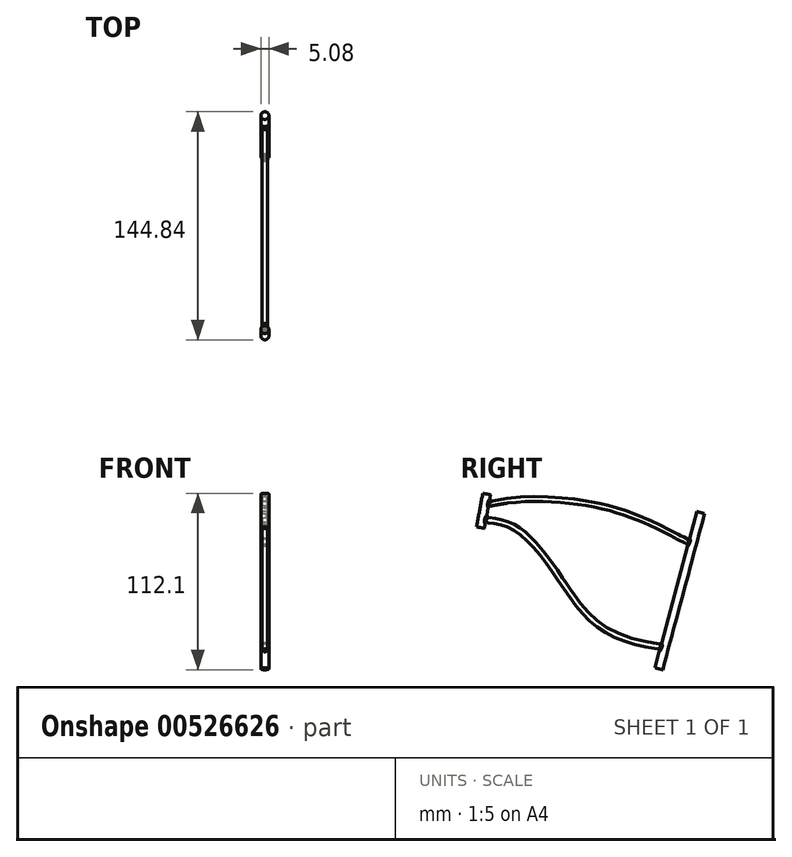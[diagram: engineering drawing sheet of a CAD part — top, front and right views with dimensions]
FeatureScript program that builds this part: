
annotation { "Feature Type Name" : "Feature", "Feature Type Description" : "" }
export const myFeature = defineFeature(function(context is Context, id is Id, definition is map)
    precondition{}
    {
        {
            var Q0;
            Q0=qCreatedBy(makeId("Right.planeOp"),FACE);
            var sketch = newSketch(context, id + "F0", { "sketchPlane" : qUnion([Q0])});
            skLineSegment(sketch, "E0", {"start": v(64.7, 35.74) * mm, "end": v(38.09, -63.45) * mm});
            skLineSegment(sketch, "E1", {"start": v(-71.22, 47.53) * mm, "end": v(-75.2, 26.24) * mm});
            skFitSpline(sketch, "E2", {"points": [v(59.3, 15.64) * mm, v(3.87, 39.19) * mm, v(-72.53, 40.51) * mm], "startDerivative": vector(-133.27, 70.5) * mm, "endDerivative": vector(-137.17, -35.71) * mm});
            skFitSpline(sketch, "E3", {"points": [v(-74.24, 31.39) * mm, v(-54.53, 26.67) * mm, v(-28.9, 0) * mm, v(-2.09, -34.12) * mm, v(41.72, -49.91) * mm], "startDerivative": vector(94.97, -12.02) * mm, "endDerivative": vector(194.9, -25.15) * mm});
            skLineSegment(sketch, "E4", {"start": v(64.7, 35.74) * mm, "end": v(81.02, 31.37) * mm});
            skLineSegment(sketch, "E5", {"start": v(64.7, 35.74) * mm, "end": v(52.13, 39.11) * mm});
            skLineSegment(sketch, "E6", {"start": v(-71.22, 47.53) * mm, "end": v(-80.57, 49.28) * mm});
            skSolve(sketch);
        }
        {
            var Q0;
            Q0=sQuery(id+"F0.wireOp",EDGE,"E1");
            extrude(context, id + "F1", {"bodyType" : ToolBodyType.SURFACE, "surfaceEntities" : qUnion([Q0]), "endBound" : BoundingType.SYMMETRIC, "depth" : 25.4 * mm, "offsetDistance" : 25.4 * mm});
        }
        {
            var Q0;
            Q0=makeQuery(id+"F1.opExtrude","SWEPT_FACE",FACE,{"disambiguationData":[OSD([sQuery(id+"F0.wireOp",EDGE,"E1")])]});
            var sketch = newSketch(context, id + "F2", { "sketchPlane" : qUnion([Q0])});
            skCircle(sketch, "E7", {"center": v(0, 26.48) * mm, "radius": 1.65 * mm});
            skCircle(sketch, "E8", {"center": v(0, 17.23) * mm, "radius": 1.65 * mm});
            skSolve(sketch);
        }
        {
            var Q0;
            Q0=makeQuery(id+"F2.imprint","IMPRINT",FACE,{"disambiguationData":[TD([[makeQuery(id+"F2.imprint","IMPRINT",EDGE,{"derivedFrom":sQuery(id+"F2.wireOp",EDGE,"E7")}),1.0]])]});
            var Q1;
            Q1=sQuery(id+"F0.wireOp",EDGE,"E2");
            sweep(context, id + "F3", {"profiles" : qUnion([Q0]), "path" : qUnion([Q1])});
        }
        {
            var Q0;
            Q0=makeQuery(id+"F2.imprint","IMPRINT",FACE,{"disambiguationData":[TD([[makeQuery(id+"F2.imprint","IMPRINT",EDGE,{"derivedFrom":sQuery(id+"F2.wireOp",EDGE,"E8")}),1.0]])]});
            var Q1;
            Q1=sQuery(id+"F0.wireOp",EDGE,"E3");
            sweep(context, id + "F4", {"profiles" : qUnion([Q0]), "path" : qUnion([Q1])});
        }
        {
            var Q0;
            Q0=sQuery(id+"F0.wireOp",EDGE,"E4");
            extrude(context, id + "F5", {"bodyType" : ToolBodyType.SURFACE, "surfaceEntities" : qUnion([Q0]), "endBound" : BoundingType.SYMMETRIC, "depth" : 25.4 * mm, "offsetDistance" : 25.4 * mm});
        }
        {
            var Q0;
            Q0=makeQuery(id+"F5.opExtrude","SWEPT_FACE",FACE,{"disambiguationData":[OSD([sQuery(id+"F0.wireOp",EDGE,"E4")])]});
            var sketch = newSketch(context, id + "F6", { "sketchPlane" : qUnion([Q0])});
            skCircle(sketch, "E9", {"center": v(0, -53.22) * mm, "radius": 2.54 * mm});
            skSolve(sketch);
        }
        {
            var Q0;
            {var subQ0=sQuery(id+"F6.wireOp",EDGE,"E9");var subQ1=makeQuery(id+"F5.opExtrude","SWEPT_EDGE",EDGE,{"disambiguationData":[OSD([sQuery(id+"F0.wireOp",VERTEX,"E4.start")])]});var subQ2=makeQuery(id+"F6.imprint","INTERSECT",VERTEX,{"disambiguationData":[OD(0.0)],"derivedFrom":[subQ1,subQ0]});Q0=makeQuery(id+"F6.imprint","IMPRINT",FACE,{"disambiguationData":[TD([[makeQuery(id+"F6.imprint","IMPRINT",EDGE,{"disambiguationData":[TD([[subQ2,1.0]])],"derivedFrom":subQ0}),1.0]])]});}
            var Q1;
            {var subQ0=sQuery(id+"F6.wireOp",EDGE,"E9");var subQ1=makeQuery(id+"F5.opExtrude","SWEPT_EDGE",EDGE,{"disambiguationData":[OSD([sQuery(id+"F0.wireOp",VERTEX,"E4.start")])]});var subQ2=makeQuery(id+"F6.imprint","INTERSECT",VERTEX,{"disambiguationData":[OD(0.0)],"derivedFrom":[subQ1,subQ0]});Q1=makeQuery(id+"F6.imprint","IMPRINT",FACE,{"disambiguationData":[TD([[makeQuery(id+"F6.imprint","IMPRINT",EDGE,{"disambiguationData":[TD([[subQ2,-1.0]])],"derivedFrom":subQ0}),1.0]])]});}
            var Q2;
            Q2=sQuery(id+"F0.wireOp",EDGE,"E0");
            sweep(context, id + "F7", {"profiles" : qUnion([Q0, Q1]), "path" : qUnion([Q2])});
        }
        {
            var Q0;
            Q0=sQuery(id+"F0.wireOp",EDGE,"E6");
            extrude(context, id + "F8", {"bodyType" : ToolBodyType.SURFACE, "surfaceEntities" : qUnion([Q0]), "endBound" : BoundingType.SYMMETRIC, "depth" : 25.4 * mm, "offsetDistance" : 25.4 * mm});
        }
        {
            var Q0;
            Q0=makeQuery(id+"F8.opExtrude","SWEPT_FACE",FACE,{"disambiguationData":[OSD([sQuery(id+"F0.wireOp",EDGE,"E6")])]});
            var sketch = newSketch(context, id + "F9", { "sketchPlane" : qUnion([Q0])});
            skCircle(sketch, "E10", {"center": v(0, -78.74) * mm, "radius": 2.54 * mm});
            skSolve(sketch);
        }
        {
            var Q0;
            {var subQ0=sQuery(id+"F9.wireOp",EDGE,"E10");var subQ1=makeQuery(id+"F8.opExtrude","SWEPT_EDGE",EDGE,{"disambiguationData":[OSD([sQuery(id+"F0.wireOp",VERTEX,"E6.start")])]});var subQ2=makeQuery(id+"F9.imprint","INTERSECT",VERTEX,{"disambiguationData":[OD(0.0)],"derivedFrom":[subQ1,subQ0]});Q0=makeQuery(id+"F9.imprint","IMPRINT",FACE,{"disambiguationData":[TD([[makeQuery(id+"F9.imprint","IMPRINT",EDGE,{"disambiguationData":[TD([[subQ2,1.0]])],"derivedFrom":subQ0}),1.0]])]});}
            var Q1;
            {var subQ0=sQuery(id+"F9.wireOp",EDGE,"E10");var subQ1=makeQuery(id+"F8.opExtrude","SWEPT_EDGE",EDGE,{"disambiguationData":[OSD([sQuery(id+"F0.wireOp",VERTEX,"E6.start")])]});var subQ2=makeQuery(id+"F9.imprint","INTERSECT",VERTEX,{"disambiguationData":[OD(0.0)],"derivedFrom":[subQ1,subQ0]});Q1=makeQuery(id+"F9.imprint","IMPRINT",FACE,{"disambiguationData":[TD([[makeQuery(id+"F9.imprint","IMPRINT",EDGE,{"disambiguationData":[TD([[subQ2,-1.0]])],"derivedFrom":subQ0}),1.0]])]});}
            var Q2;
            Q2=sQuery(id+"F0.wireOp",EDGE,"E1");
            sweep(context, id + "F10", {"profiles" : qUnion([Q0, Q1]), "path" : qUnion([Q2])});
        }
        {
            var Q0;
            Q0=makeQuery(id+"F3.opSweep","SWEPT_BODY",BODY,{"disambiguationData":[OSD([sQuery(id+"F0.wireOp",EDGE,"E2"),sQuery(id+"F2.wireOp",EDGE,"E7")])]});
            var Q1;
            Q1=makeQuery(id+"F10.opSweep","SWEPT_BODY",BODY,{"disambiguationData":[OSD([sQuery(id+"F0.wireOp",EDGE,"E1"),sQuery(id+"F9.wireOp",EDGE,"E10")])]});
            var Q2;
            Q2=makeQuery(id+"F4.opSweep","SWEPT_BODY",BODY,{"disambiguationData":[OSD([sQuery(id+"F0.wireOp",EDGE,"E3"),sQuery(id+"F2.wireOp",EDGE,"E8")])]});
            var Q3;
            Q3=makeQuery(id+"F7.opSweep","SWEPT_BODY",BODY,{"disambiguationData":[OSD([sQuery(id+"F0.wireOp",EDGE,"E0"),sQuery(id+"F6.wireOp",EDGE,"E9")])]});
            booleanBodies(context, id + "F11", {"operationType" : BooleanOperationType.UNION, "tools" : qUnion([Q0, Q1, Q2, Q3])});
        }
        {
            var Q0;
            Q0=makeQuery(id+"F11.opBoolean","INTERSECT",EDGE,{"derivedFrom":[makeQuery(id+"F4.opSweep","SWEPT_FACE",FACE,{"disambiguationData":[OSD([sQuery(id+"F0.wireOp",EDGE,"E3"),sQuery(id+"F2.wireOp",EDGE,"E8")])]}),makeQuery(id+"F10.opSweep","SWEPT_FACE",FACE,{"disambiguationData":[OSD([sQuery(id+"F0.wireOp",EDGE,"E1"),sQuery(id+"F9.wireOp",EDGE,"E10")])]})]});
            var Q1;
            Q1=makeQuery(id+"F11.opBoolean","INTERSECT",EDGE,{"derivedFrom":[makeQuery(id+"F3.opSweep","SWEPT_FACE",FACE,{"disambiguationData":[OSD([sQuery(id+"F0.wireOp",EDGE,"E2"),sQuery(id+"F2.wireOp",EDGE,"E7")])]}),makeQuery(id+"F7.opSweep","SWEPT_FACE",FACE,{"disambiguationData":[OSD([sQuery(id+"F0.wireOp",EDGE,"E0"),sQuery(id+"F6.wireOp",EDGE,"E9")])]})]});
            var Q2;
            Q2=makeQuery(id+"F11.opBoolean","INTERSECT",EDGE,{"derivedFrom":[makeQuery(id+"F4.opSweep","SWEPT_FACE",FACE,{"disambiguationData":[OSD([sQuery(id+"F0.wireOp",EDGE,"E3"),sQuery(id+"F2.wireOp",EDGE,"E8")])]}),makeQuery(id+"F7.opSweep","SWEPT_FACE",FACE,{"disambiguationData":[OSD([sQuery(id+"F0.wireOp",EDGE,"E0"),sQuery(id+"F6.wireOp",EDGE,"E9")])]})]});
            var Q3;
            Q3=makeQuery(id+"F11.opBoolean","INTERSECT",EDGE,{"derivedFrom":[makeQuery(id+"F3.opSweep","SWEPT_FACE",FACE,{"disambiguationData":[OSD([sQuery(id+"F0.wireOp",EDGE,"E2"),sQuery(id+"F2.wireOp",EDGE,"E7")])]}),makeQuery(id+"F10.opSweep","SWEPT_FACE",FACE,{"disambiguationData":[OSD([sQuery(id+"F0.wireOp",EDGE,"E1"),sQuery(id+"F9.wireOp",EDGE,"E10")])]})]});
            fillet(context, id + "F12", {"entities" : qUnion([Q0, Q1, Q2, Q3]), "radius" : 1.47 * mm, "tangentPropagation" : true, "allowEdgeOverflow" : false});
        }
    });
